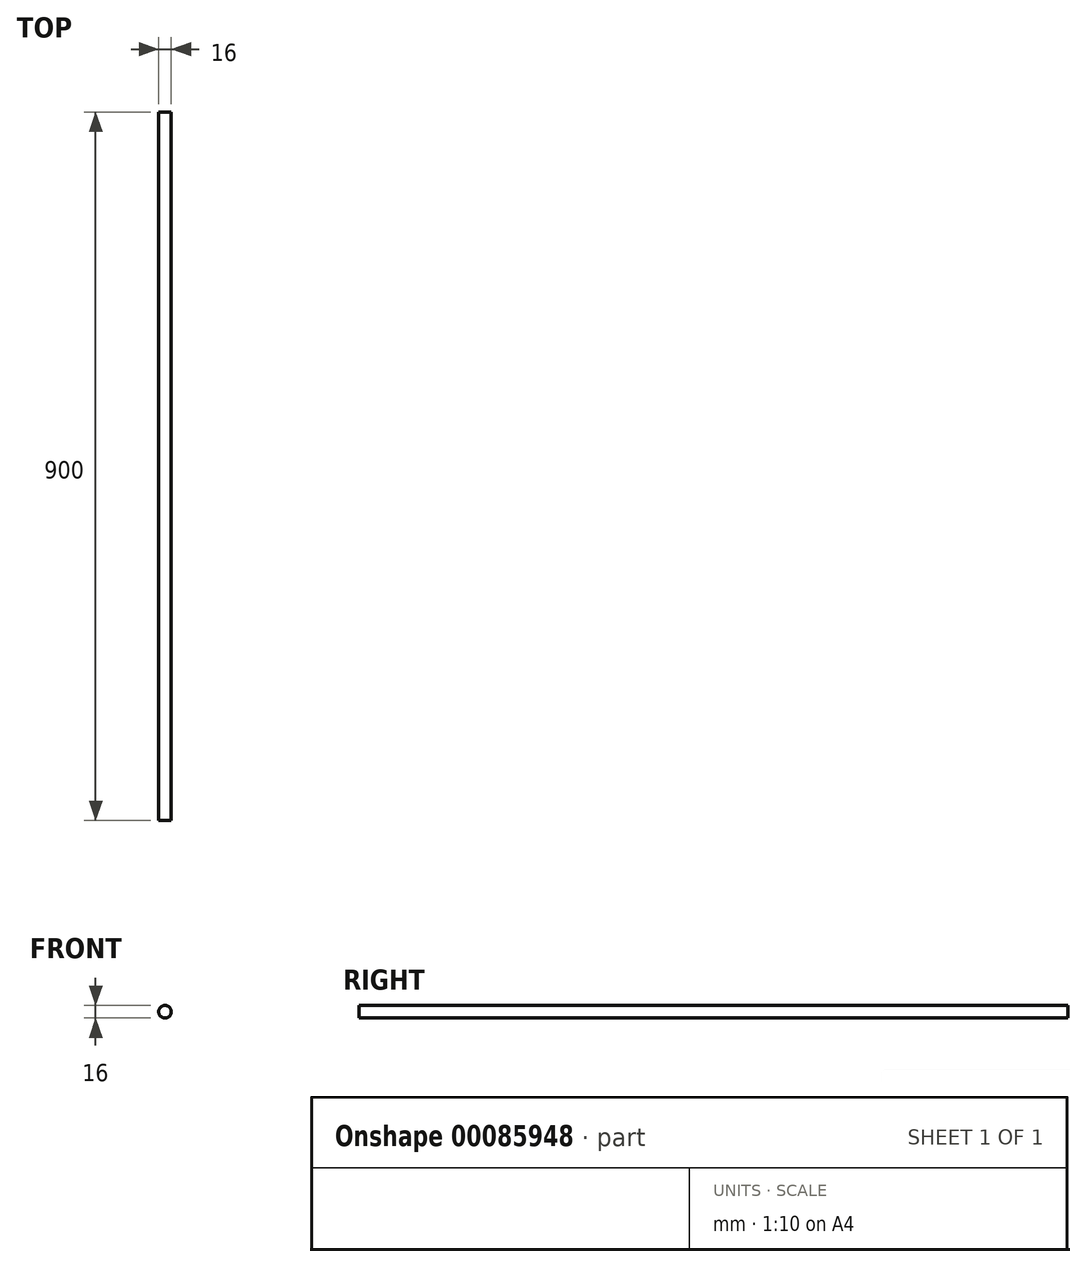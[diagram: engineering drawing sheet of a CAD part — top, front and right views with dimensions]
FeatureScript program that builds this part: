
annotation { "Feature Type Name" : "Feature", "Feature Type Description" : "" }
export const myFeature = defineFeature(function(context is Context, id is Id, definition is map)
    precondition{}
    {
        {
            var Q0;
            Q0=qCreatedBy(makeId("Front.planeOp"),FACE);
            var sketch = newSketch(context, id + "F0", { "sketchPlane" : qUnion([Q0])});
            skCircle(sketch, "E0", {"center": v(-60.58, 51.96) * mm, "radius": 8 * mm});
            skSolve(sketch);
        }
        {
            var Q0;
            Q0 = qSketchRegion(id + "F0", true);
            extrude(context, id + "F1", {"entities" : qUnion([Q0]), "depth" : 900 * mm});
        }
    });
